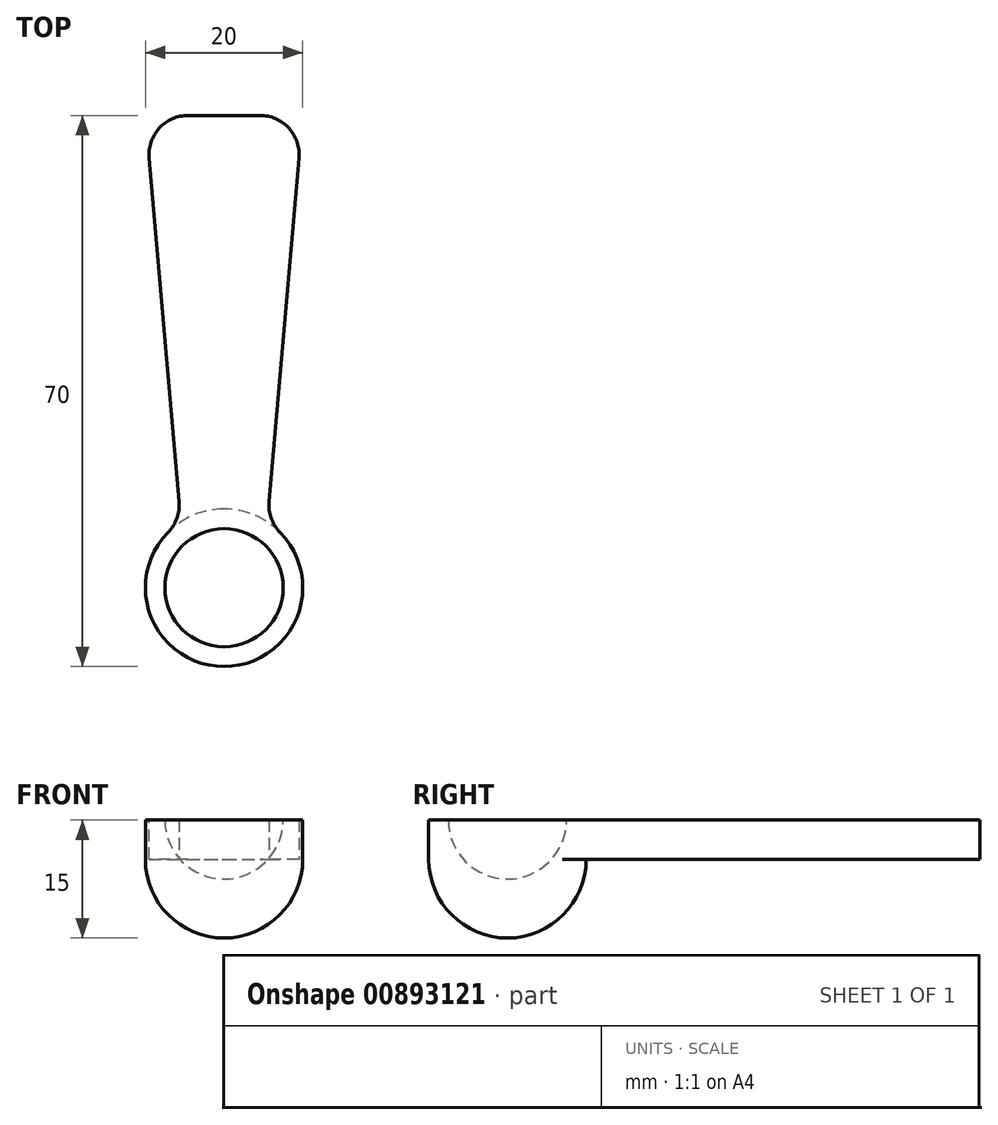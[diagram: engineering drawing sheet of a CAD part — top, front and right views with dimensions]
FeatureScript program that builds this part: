
annotation { "Feature Type Name" : "Feature", "Feature Type Description" : "" }
export const myFeature = defineFeature(function(context is Context, id is Id, definition is map)
    precondition{}
    {
        {
            var Q0;
            Q0=qCreatedBy(makeId("Top.planeOp"),FACE);
            var sketch = newSketch(context, id + "F0", { "sketchPlane" : qUnion([Q0])});
            skCircle(sketch, "E0", {"center": v(0, 0) * mm, "radius": 10 * mm});
            skLineSegment(sketch, "E1", {"start": v(0, 0) * mm, "end": v(0, 60) * mm, "construction": true});
            skLineSegment(sketch, "E2", {"start": v(0, 60) * mm, "end": v(-10, 60) * mm});
            skLineSegment(sketch, "E3", {"start": v(-10, 60) * mm, "end": v(-5.48, 8.36) * mm});
            skLineSegment(sketch, "E4.MirrorCS", {"start": v(0, 60) * mm, "end": v(10, 60) * mm});
            skLineSegment(sketch, "E5.MirrorCS", {"start": v(10, 60) * mm, "end": v(5.48, 8.36) * mm});
            skSolve(sketch);
        }
        {
            var Q0;
            Q0 = qSketchRegion(id + "F0", true);
            extrude(context, id + "F1", {"entities" : qUnion([Q0]), "depth" : 5 * mm, "offsetDistance" : 25 * mm});
        }
        {
            var Q0;
            Q0=makeQuery(id+"F1.opExtrude","CAP_FACE",FACE,{"disambiguationData":[OSD([sQuery(id+"F0.wireOp",EDGE,"E0"),sQuery(id+"F0.wireOp",EDGE,"E2"),sQuery(id+"F0.wireOp",EDGE,"E3"),sQuery(id+"F0.wireOp",EDGE,"E4.MirrorCS"),sQuery(id+"F0.wireOp",EDGE,"E5.MirrorCS")])],"isStart":true});
            var sketch = newSketch(context, id + "F2", { "sketchPlane" : qUnion([Q0])});
            skCircle(sketch, "E6", {"center": v(0, 0) * mm, "radius": 10 * mm});
            skLineSegment(sketch, "E7", {"start": v(0, 10) * mm, "end": v(0, -10) * mm});
            skSolve(sketch);
        }
        {
            var Q0;
            {var subQ2=sQuery(id+"F2.wireOp",EDGE,"E7");Q0=makeQuery(id+"F2.imprint","IMPRINT",FACE,{"disambiguationData":[TD([[makeQuery(id+"F2.imprint","IMPRINT",EDGE,{"derivedFrom":subQ2}),1.0]])]});}
            var Q1;
            Q1=sQuery(id+"F2.wireOp",EDGE,"E7");
            revolve(context, id + "F3", {"operationType" : NewBodyOperationType.ADD, "surfaceOperationType" : NewSurfaceOperationType.NEW, "entities" : qUnion([Q0]), "axis" : qUnion([Q1]), "revolveType" : RevolveType.ONE_DIRECTION, "angle" : 180 * degree});
        }
        {
            var Q0;
            Q0=makeQuery(id+"F1.opExtrude","CAP_FACE",FACE,{"disambiguationData":[OSD([sQuery(id+"F0.wireOp",EDGE,"E0"),sQuery(id+"F0.wireOp",EDGE,"E2"),sQuery(id+"F0.wireOp",EDGE,"E3"),sQuery(id+"F0.wireOp",EDGE,"E4.MirrorCS"),sQuery(id+"F0.wireOp",EDGE,"E5.MirrorCS")])],"isStart":false});
            var sketch = newSketch(context, id + "F4", { "sketchPlane" : qUnion([Q0])});
            skCircle(sketch, "E8", {"center": v(0, 0) * mm, "radius": 7.5 * mm});
            skLineSegment(sketch, "E9", {"start": v(0, -7.5) * mm, "end": v(0, 7.5) * mm});
            skSolve(sketch);
        }
        {
            var Q0;
            {var subQ0=sQuery(id+"F4.wireOp",EDGE,"E9");Q0=makeQuery(id+"F4.imprint","IMPRINT",FACE,{"disambiguationData":[TD([[makeQuery(id+"F4.imprint","IMPRINT",EDGE,{"derivedFrom":subQ0}),1.0]])]});}
            var Q1;
            Q1=sQuery(id+"F4.wireOp",EDGE,"E9");
            revolve(context, id + "F5", {"operationType" : NewBodyOperationType.REMOVE, "surfaceOperationType" : NewSurfaceOperationType.NEW, "entities" : qUnion([Q0]), "axis" : qUnion([Q1]), "revolveType" : RevolveType.ONE_DIRECTION, "oppositeDirection" : true, "angle" : 180 * degree});
        }
        {
            var Q0;
            Q0=makeQuery(id+"F1.opExtrude","SWEPT_EDGE",EDGE,{"disambiguationData":[OSD([sQuery(id+"F0.wireOp",EDGE,"E4.MirrorCS"),sQuery(id+"F0.wireOp",EDGE,"E5.MirrorCS")])]});
            var Q1;
            Q1=makeQuery(id+"F1.opExtrude","SWEPT_EDGE",EDGE,{"disambiguationData":[OSD([sQuery(id+"F0.wireOp",EDGE,"E2"),sQuery(id+"F0.wireOp",EDGE,"E3")])]});
            var Q2;
            Q2=makeQuery(id+"F3.boolean.opBoolean","SPLIT",EDGE,{"derivedFrom":makeQuery(id+"F3.opRevolve","CAP_EDGE",EDGE,{"disambiguationData":[OSD([sQuery(id+"F2.wireOp",EDGE,"E6")])],"isStart":true})});
            fillet(context, id + "F6", {"entities" : qUnion([Q0, Q1, Q2]), "radius" : 5 * mm, "tangentPropagation" : true, "allowEdgeOverflow" : false});
        }
        {
            var Q0;
            Q0=makeQuery(id+"F1.opExtrude","SWEPT_EDGE",EDGE,{"disambiguationData":[OSD([sQuery(id+"F0.wireOp",EDGE,"E0"),sQuery(id+"F0.wireOp",EDGE,"E5.MirrorCS")])]});
            fillet(context, id + "F7", {"entities" : qUnion([Q0]), "radius" : 5 * mm, "tangentPropagation" : true, "allowEdgeOverflow" : false});
        }
        {
            var Q0;
            Q0=makeQuery(id+"F1.opExtrude","SWEPT_EDGE",EDGE,{"disambiguationData":[OSD([sQuery(id+"F0.wireOp",EDGE,"E0"),sQuery(id+"F0.wireOp",EDGE,"E3")])]});
            fillet(context, id + "F8", {"entities" : qUnion([Q0]), "radius" : 5 * mm, "tangentPropagation" : true, "allowEdgeOverflow" : false});
        }
    });
